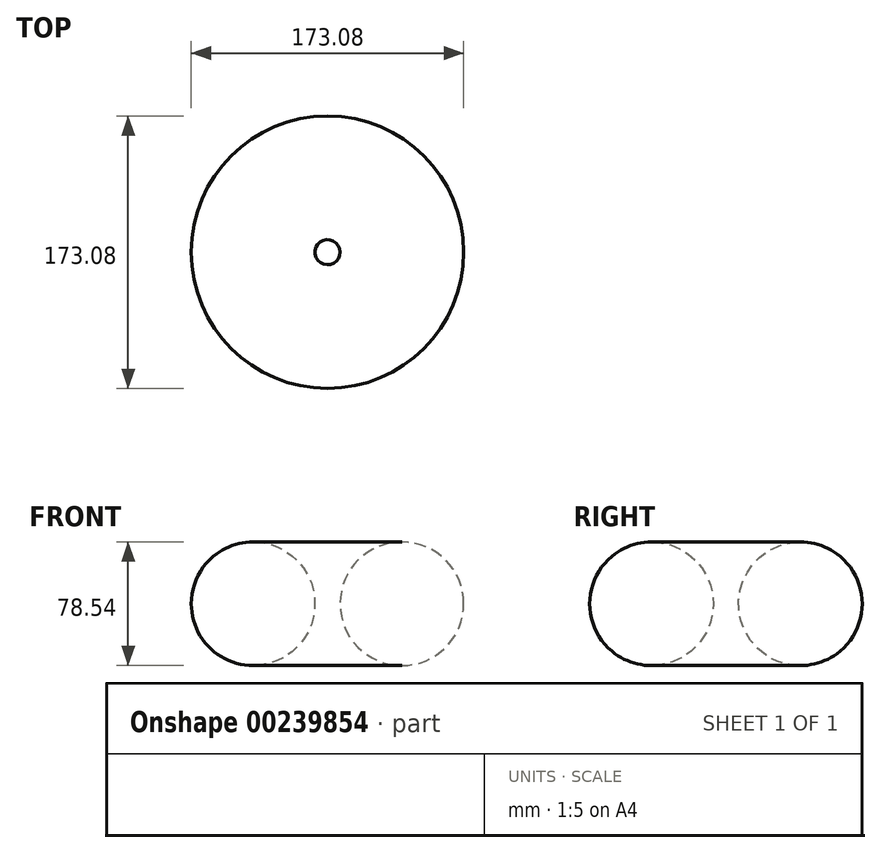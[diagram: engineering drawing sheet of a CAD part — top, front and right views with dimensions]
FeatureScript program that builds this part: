
annotation { "Feature Type Name" : "Feature", "Feature Type Description" : "" }
export const myFeature = defineFeature(function(context is Context, id is Id, definition is map)
    precondition{}
    {
        {
            var Q0;
            Q0=qCreatedBy(makeId("Front.planeOp"),FACE);
            var sketch = newSketch(context, id + "F0", { "sketchPlane" : qUnion([Q0])});
            skCircle(sketch, "E0", {"center": v(-47.27, 0) * mm, "radius": 39.27 * mm});
            skLineSegment(sketch, "E1", {"start": v(0, 38.25) * mm, "end": v(0, -34.9) * mm, "construction": true});
            skSolve(sketch);
        }
        {
            var Q0;
            Q0=makeQuery(id+"F0.imprint","IMPRINT",FACE,{"disambiguationData":[TD([[makeQuery(id+"F0.imprint","IMPRINT",EDGE,{"derivedFrom":sQuery(id+"F0.wireOp",EDGE,"E0")}),1.0]])]});
            var Q1;
            Q1=sQuery(id+"F0.wireOp",EDGE,"E1");
            revolve(context, id + "F1", {"entities" : qUnion([Q0]), "axis" : qUnion([Q1]), "revolveType" : RevolveType.FULL});
        }
    });
